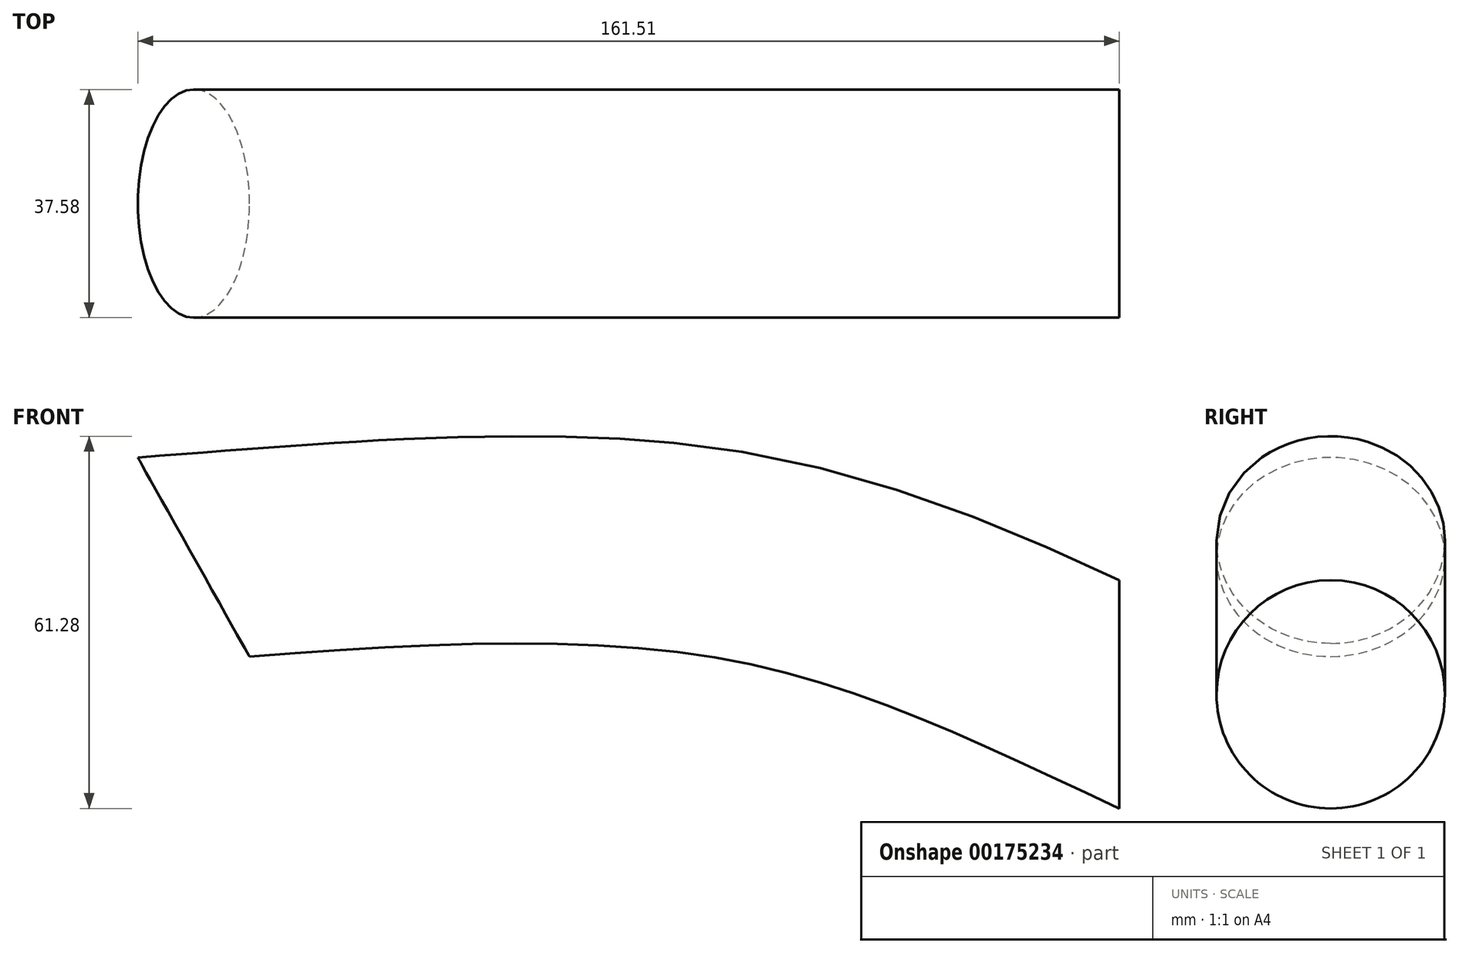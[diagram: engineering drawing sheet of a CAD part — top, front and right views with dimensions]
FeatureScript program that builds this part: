
annotation { "Feature Type Name" : "Feature", "Feature Type Description" : "" }
export const myFeature = defineFeature(function(context is Context, id is Id, definition is map)
    precondition{}
    {
        {
            var Q0;
            Q0=qCreatedBy(makeId("Front.planeOp"),FACE);
            var sketch = newSketch(context, id + "F0", { "sketchPlane" : qUnion([Q0])});
            skFitSpline(sketch, "E0", {"points": [v(-87.04, 21.43) * mm, v(-26.51, 38.22) * mm, v(45.95, 16.13) * mm, v(107.81, 47.5) * mm], "startDerivative": vector(184.77, 92.82) * mm, "endDerivative": vector(178.33, 143.21) * mm});
            skSolve(sketch);
        }
        {
            var Q0;
            Q0=qCreatedBy(makeId("Front.planeOp"),FACE);
            var sketch = newSketch(context, id + "F1", { "sketchPlane" : qUnion([Q0])});
            skFitSpline(sketch, "E1", {"points": [v(-110.84, -41.16) * mm, v(-57.71, -18.72) * mm, v(-57.34, -18.72) * mm], "startDerivative": vector(81.65, 35.48) * mm, "endDerivative": vector(3.07, -0.9) * mm});
            skFitSpline(sketch, "E2", {"points": [v(-57.34, -18.72) * mm, v(30.59, -18.72) * mm, v(94.2, -41.54) * mm], "startDerivative": vector(172.69, 13.02) * mm, "endDerivative": vector(129.42, -60.27) * mm});
            skSolve(sketch);
        }
        {
            var Q0;
            Q0=qCreatedBy(makeId("Right.planeOp"),FACE);
            var Q1;
            Q1=sQuery(id+"F1.wireOp",VERTEX,"E2.2.internal");
            cPlane(context, id + "F2", {"entities" : qUnion([Q0, Q1]), "cplaneType" : CPlaneType.PLANE_POINT, "offset" : 25.4 * mm, "width" : 152.4 * mm, "height" : 152.4 * mm});
        }
        {
            var Q0;
            Q0=qCreatedBy(id+"F2.planeOp",FACE);
            var sketch = newSketch(context, id + "F3", { "sketchPlane" : qUnion([Q0])});
            skCircle(sketch, "E3", {"center": v(0, -39.9) * mm, "radius": 18.79 * mm});
            skSolve(sketch);
        }
        {
            var Q0;
            Q0=makeQuery(id+"F3.imprint","IMPRINT",FACE,{"disambiguationData":[TD([[makeQuery(id+"F3.imprint","IMPRINT",EDGE,{"derivedFrom":sQuery(id+"F3.wireOp",EDGE,"E3")}),1.0]])]});
            var Q1;
            Q1=sQuery(id+"F1.wireOp",EDGE,"E2");
            sweep(context, id + "F4", {"profiles" : qUnion([Q0]), "path" : qUnion([Q1])});
        }
    });
